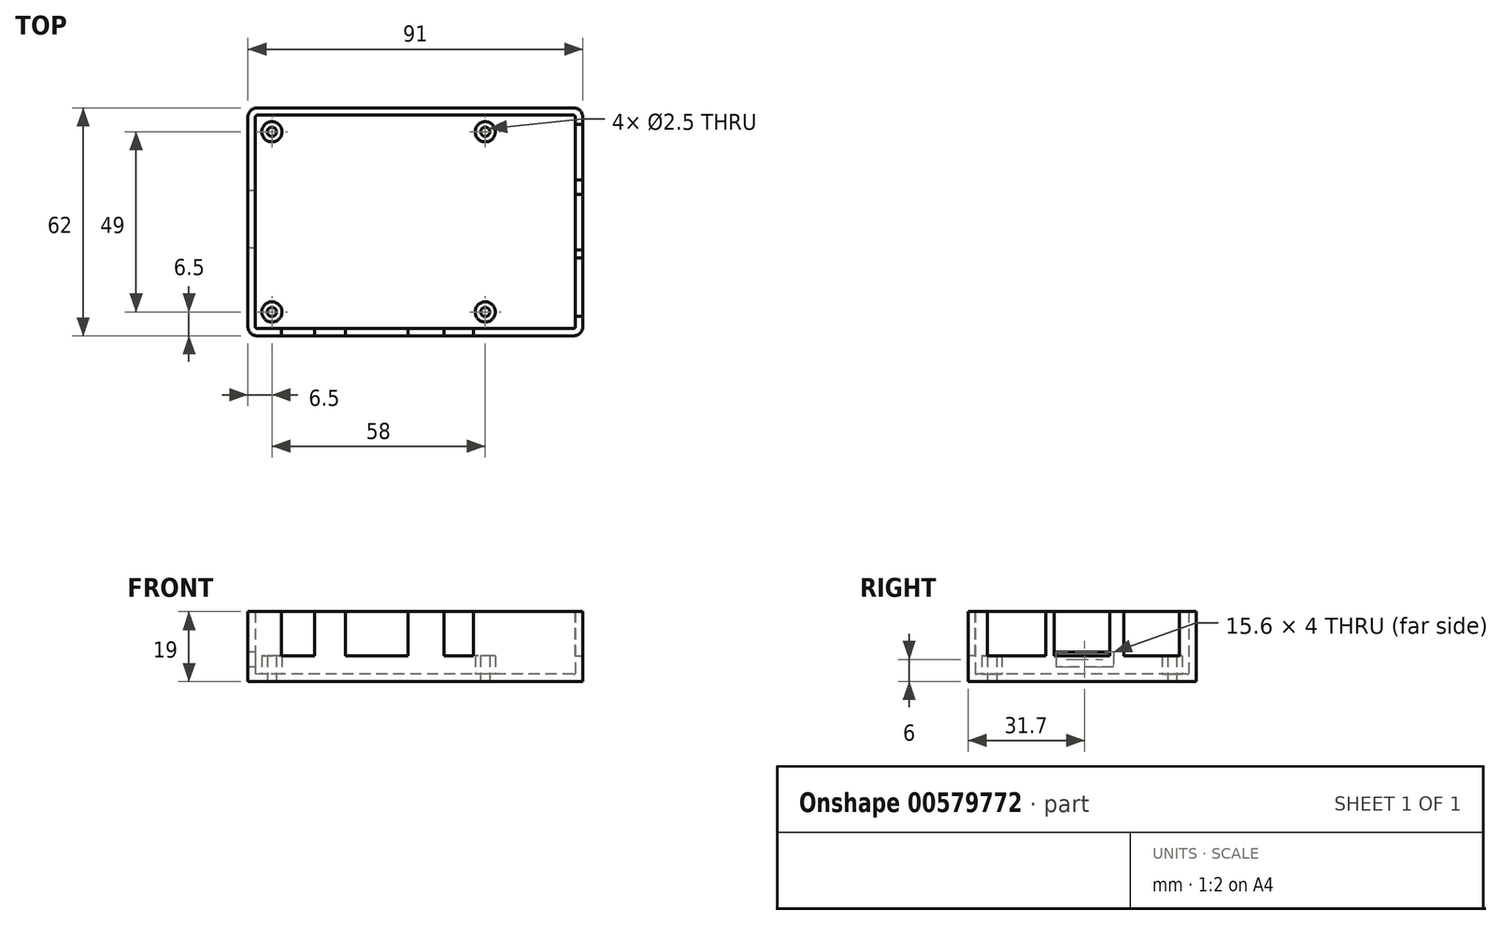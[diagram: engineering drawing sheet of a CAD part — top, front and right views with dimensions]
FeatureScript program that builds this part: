
annotation { "Feature Type Name" : "Feature", "Feature Type Description" : "" }
export const myFeature = defineFeature(function(context is Context, id is Id, definition is map)
    precondition{}
    {
        {
            var Q0;
            Q0=qCreatedBy(makeId("Top.planeOp"),FACE);
            var sketch = newSketch(context, id + "F0", { "sketchPlane" : qUnion([Q0])});
            skLineSegment(sketch, "E0.bottom", {"start": v(2.5, 0) * mm, "end": v(88.5, 0) * mm});
            skLineSegment(sketch, "E0.top", {"start": v(2.5, 62) * mm, "end": v(88.5, 62) * mm});
            skLineSegment(sketch, "E0.left", {"start": v(0, 2.5) * mm, "end": v(0, 59.5) * mm});
            skLineSegment(sketch, "E0.right", {"start": v(91, 2.5) * mm, "end": v(91, 59.5) * mm});
            skPoint(sketch, "E1.visualSharp", {"position": v(0, 62) * mm});
            skArc(sketch, "E1.filletArc", {"start": v(2.5, 62) * mm, "mid": v(0.73, 61.27) * mm, "end": v(0, 59.5) * mm});
            skPoint(sketch, "E2.visualSharp", {"position": v(91, 62) * mm});
            skArc(sketch, "E2.filletArc", {"start": v(91, 59.5) * mm, "mid": v(90.27, 61.27) * mm, "end": v(88.5, 62) * mm});
            skPoint(sketch, "E3.visualSharp", {"position": v(91, 0) * mm});
            skArc(sketch, "E3.filletArc", {"start": v(88.5, 0) * mm, "mid": v(90.27, 0.73) * mm, "end": v(91, 2.5) * mm});
            skPoint(sketch, "E4.visualSharp", {"position": v(0, 0) * mm});
            skArc(sketch, "E4.filletArc", {"start": v(0, 2.5) * mm, "mid": v(0.73, 0.73) * mm, "end": v(2.5, 0) * mm});
            skLineSegment(sketch, "E5.0", {"start": v(2, 2) * mm, "end": v(2, 60) * mm});
            skLineSegment(sketch, "E5.1", {"start": v(2, 2) * mm, "end": v(89, 2) * mm});
            skLineSegment(sketch, "E5.2", {"start": v(89, 2) * mm, "end": v(89, 60) * mm});
            skLineSegment(sketch, "E5.3", {"start": v(2, 60) * mm, "end": v(89, 60) * mm});
            skSolve(sketch);
        }
        {
            var Q0;
            Q0=makeQuery(id+"F0.imprint","IMPRINT",FACE,{"disambiguationData":[TD([[makeQuery(id+"F0.imprint","IMPRINT",EDGE,{"derivedFrom":sQuery(id+"F0.wireOp",EDGE,"E5.0")}),-1.0]])]});
            var Q1;
            Q1=makeQuery(id+"F0.imprint","IMPRINT",FACE,{"disambiguationData":[TD([[makeQuery(id+"F0.imprint","IMPRINT",EDGE,{"derivedFrom":sQuery(id+"F0.wireOp",EDGE,"E0.bottom")}),1.0]])]});
            extrude(context, id + "F1", {"entities" : qUnion([Q0, Q1]), "depth" : 2 * mm, "offsetDistance" : 25 * mm});
        }
        {
            var Q0;
            Q0 = qSketchRegion(id + "F0", true);
            extrude(context, id + "F2", {"entities" : qUnion([Q0]), "operationType" : NewBodyOperationType.ADD, "depth" : 19 * mm, "offsetDistance" : 25 * mm});
        }
        {
            var Q0;
            Q0=makeQuery(id+"F1.opExtrude","CAP_FACE",FACE,{"disambiguationData":[OSD([sQuery(id+"F0.wireOp",EDGE,"E0.bottom"),sQuery(id+"F0.wireOp",EDGE,"E0.top"),sQuery(id+"F0.wireOp",EDGE,"E0.left"),sQuery(id+"F0.wireOp",EDGE,"E0.right"),sQuery(id+"F0.wireOp",EDGE,"E1.filletArc"),sQuery(id+"F0.wireOp",EDGE,"E2.filletArc"),sQuery(id+"F0.wireOp",EDGE,"E3.filletArc"),sQuery(id+"F0.wireOp",EDGE,"E4.filletArc")])],"isStart":false});
            var sketch = newSketch(context, id + "F3", { "sketchPlane" : qUnion([Q0])});
            skCircle(sketch, "E6", {"center": v(6.5, 55.5) * mm, "radius": 2.75 * mm});
            skCircle(sketch, "E7", {"center": v(64.5, 6.5) * mm, "radius": 2.75 * mm});
            skCircle(sketch, "E8", {"center": v(6.5, 6.5) * mm, "radius": 2.75 * mm});
            skCircle(sketch, "E9", {"center": v(64.5, 55.5) * mm, "radius": 2.75 * mm});
            skCircle(sketch, "E10", {"center": v(6.5, 55.5) * mm, "radius": 1.25 * mm});
            skCircle(sketch, "E11", {"center": v(64.5, 55.5) * mm, "radius": 1.25 * mm});
            skCircle(sketch, "E12", {"center": v(64.5, 6.5) * mm, "radius": 1.25 * mm});
            skCircle(sketch, "E13", {"center": v(6.5, 6.5) * mm, "radius": 1.25 * mm});
            skSolve(sketch);
        }
        {
            var Q0;
            Q0 = qSketchRegion(id + "F3", true);
            extrude(context, id + "F4", {"entities" : qUnion([Q0]), "operationType" : NewBodyOperationType.ADD, "depth" : 5 * mm, "offsetDistance" : 25 * mm});
        }
        {
            var Q0;
            Q0=makeQuery(id+"F2.opExtrude","CAP_FACE",FACE,{"disambiguationData":[OSD([sQuery(id+"F0.wireOp",EDGE,"E0.bottom"),sQuery(id+"F0.wireOp",EDGE,"E0.top"),sQuery(id+"F0.wireOp",EDGE,"E0.left"),sQuery(id+"F0.wireOp",EDGE,"E0.right"),sQuery(id+"F0.wireOp",EDGE,"E1.filletArc"),sQuery(id+"F0.wireOp",EDGE,"E2.filletArc"),sQuery(id+"F0.wireOp",EDGE,"E3.filletArc"),sQuery(id+"F0.wireOp",EDGE,"E4.filletArc"),sQuery(id+"F0.wireOp",EDGE,"E5.0"),sQuery(id+"F0.wireOp",EDGE,"E5.1"),sQuery(id+"F0.wireOp",EDGE,"E5.2"),sQuery(id+"F0.wireOp",EDGE,"E5.3")])],"isStart":false});
            var sketch = newSketch(context, id + "F5", { "sketchPlane" : qUnion([Q0])});
            skLineSegment(sketch, "E14.bottom", {"start": v(9.05, 0) * mm, "end": v(18.05, 0) * mm});
            skLineSegment(sketch, "E14.top", {"start": v(9.05, 2) * mm, "end": v(18.05, 2) * mm});
            skLineSegment(sketch, "E14.left", {"start": v(9.05, 0) * mm, "end": v(9.05, 2) * mm});
            skLineSegment(sketch, "E14.right", {"start": v(18.05, 0) * mm, "end": v(18.05, 2) * mm});
            skLineSegment(sketch, "E15.bottom", {"start": v(26.5, 2) * mm, "end": v(43.5, 2) * mm});
            skLineSegment(sketch, "E15.top", {"start": v(26.5, 0) * mm, "end": v(43.5, 0) * mm});
            skLineSegment(sketch, "E15.left", {"start": v(26.5, 2) * mm, "end": v(26.5, 0) * mm});
            skLineSegment(sketch, "E15.right", {"start": v(43.5, 2) * mm, "end": v(43.5, 0) * mm});
            skLineSegment(sketch, "E16.bottom", {"start": v(53.25, 2) * mm, "end": v(61.25, 2) * mm});
            skLineSegment(sketch, "E16.top", {"start": v(53.25, 0) * mm, "end": v(61.25, 0) * mm});
            skLineSegment(sketch, "E16.left", {"start": v(53.25, 2) * mm, "end": v(53.25, 0) * mm});
            skLineSegment(sketch, "E16.right", {"start": v(61.25, 2) * mm, "end": v(61.25, 0) * mm});
            skLineSegment(sketch, "E17.bottom", {"start": v(89, 21.2) * mm, "end": v(91, 21.2) * mm});
            skLineSegment(sketch, "E17.top", {"start": v(89, 5.3) * mm, "end": v(91, 5.3) * mm});
            skLineSegment(sketch, "E17.left", {"start": v(89, 21.2) * mm, "end": v(89, 5.3) * mm});
            skLineSegment(sketch, "E17.right", {"start": v(91, 21.2) * mm, "end": v(91, 5.3) * mm});
            skLineSegment(sketch, "E18.bottom", {"start": v(89, 23.4) * mm, "end": v(91, 23.4) * mm});
            skLineSegment(sketch, "E18.top", {"start": v(89, 38.5) * mm, "end": v(91, 38.5) * mm});
            skLineSegment(sketch, "E18.left", {"start": v(89, 23.4) * mm, "end": v(89, 38.5) * mm});
            skLineSegment(sketch, "E18.right", {"start": v(91, 23.4) * mm, "end": v(91, 38.5) * mm});
            skLineSegment(sketch, "E19.bottom", {"start": v(89, 42.4) * mm, "end": v(91, 42.4) * mm});
            skLineSegment(sketch, "E19.top", {"start": v(89, 57.5) * mm, "end": v(91, 57.5) * mm});
            skLineSegment(sketch, "E19.left", {"start": v(89, 42.4) * mm, "end": v(89, 57.5) * mm});
            skLineSegment(sketch, "E19.right", {"start": v(91, 42.4) * mm, "end": v(91, 57.5) * mm});
            skSolve(sketch);
        }
        {
            var Q0;
            Q0 = qSketchRegion(id + "F5", true);
            extrude(context, id + "F6", {"entities" : qUnion([Q0]), "operationType" : NewBodyOperationType.REMOVE, "oppositeDirection" : true, "depth" : 12 * mm, "offsetDistance" : 25 * mm});
        }
        {
            var Q0;
            {var subQ0=sQuery(id+"F0.wireOp",EDGE,"E0.left");Q0=makeQuery(id+"F2.boolean.opBoolean","MERGE",FACE,{"derivedFrom":[makeQuery(id+"F1.opExtrude","SWEPT_FACE",FACE,{"disambiguationData":[OSD([subQ0])]}),makeQuery(id+"F2.opExtrude","SWEPT_FACE",FACE,{"disambiguationData":[OSD([subQ0])]})]});}
            var sketch = newSketch(context, id + "F7", { "sketchPlane" : qUnion([Q0])});
            skLineSegment(sketch, "E20.bottom", {"start": v(-39.5, 8) * mm, "end": v(-23.9, 8) * mm});
            skLineSegment(sketch, "E20.top", {"start": v(-39.5, 4) * mm, "end": v(-23.9, 4) * mm});
            skLineSegment(sketch, "E20.left", {"start": v(-39.5, 8) * mm, "end": v(-39.5, 4) * mm});
            skLineSegment(sketch, "E20.right", {"start": v(-23.9, 8) * mm, "end": v(-23.9, 4) * mm});
            skSolve(sketch);
        }
        {
            var Q0;
            Q0 = qSketchRegion(id + "F7", true);
            extrude(context, id + "F8", {"entities" : qUnion([Q0]), "operationType" : NewBodyOperationType.REMOVE, "oppositeDirection" : true, "depth" : 5 * mm, "offsetDistance" : 25 * mm});
        }
        {
            var Q0;
            Q0=makeQuery(id+"F2.opExtrude","SWEPT_EDGE",EDGE,{"disambiguationData":[OSD([sQuery(id+"F0.wireOp",EDGE,"E5.0"),sQuery(id+"F0.wireOp",EDGE,"E5.3")])]});
            var Q1;
            Q1=makeQuery(id+"F2.opExtrude","SWEPT_EDGE",EDGE,{"disambiguationData":[OSD([sQuery(id+"F0.wireOp",EDGE,"E5.2"),sQuery(id+"F0.wireOp",EDGE,"E5.3")])]});
            var Q2;
            Q2=makeQuery(id+"F2.opExtrude","SWEPT_EDGE",EDGE,{"disambiguationData":[OSD([sQuery(id+"F0.wireOp",EDGE,"E5.0"),sQuery(id+"F0.wireOp",EDGE,"E5.1")])]});
            var Q3;
            Q3=makeQuery(id+"F2.opExtrude","SWEPT_EDGE",EDGE,{"disambiguationData":[OSD([sQuery(id+"F0.wireOp",EDGE,"E5.1"),sQuery(id+"F0.wireOp",EDGE,"E5.2")])]});
            fillet(context, id + "F9", {"entities" : qUnion([Q0, Q1, Q2, Q3]), "radius" : 0.5 * mm, "tangentPropagation" : true, "allowEdgeOverflow" : false});
        }
        {
            var Q0;
            Q0=makeQuery(id+"F4.boolean.opBoolean","SPLIT",FACE,{"disambiguationData":[TD([makeQuery(id+"F4.opExtrude","SWEPT_FACE",FACE,{"disambiguationData":[OSD([sQuery(id+"F3.wireOp",EDGE,"E10")])]})])],"derivedFrom":makeQuery(id+"F1.opExtrude","CAP_FACE",FACE,{"disambiguationData":[OSD([sQuery(id+"F0.wireOp",EDGE,"E0.bottom"),sQuery(id+"F0.wireOp",EDGE,"E0.top"),sQuery(id+"F0.wireOp",EDGE,"E0.left"),sQuery(id+"F0.wireOp",EDGE,"E0.right"),sQuery(id+"F0.wireOp",EDGE,"E1.filletArc"),sQuery(id+"F0.wireOp",EDGE,"E2.filletArc"),sQuery(id+"F0.wireOp",EDGE,"E3.filletArc"),sQuery(id+"F0.wireOp",EDGE,"E4.filletArc")])],"isStart":false})});
            var Q1;
            Q1=makeQuery(id+"F4.boolean.opBoolean","SPLIT",FACE,{"disambiguationData":[TD([makeQuery(id+"F4.opExtrude","SWEPT_FACE",FACE,{"disambiguationData":[OSD([sQuery(id+"F3.wireOp",EDGE,"E11")])]})])],"derivedFrom":makeQuery(id+"F1.opExtrude","CAP_FACE",FACE,{"disambiguationData":[OSD([sQuery(id+"F0.wireOp",EDGE,"E0.bottom"),sQuery(id+"F0.wireOp",EDGE,"E0.top"),sQuery(id+"F0.wireOp",EDGE,"E0.left"),sQuery(id+"F0.wireOp",EDGE,"E0.right"),sQuery(id+"F0.wireOp",EDGE,"E1.filletArc"),sQuery(id+"F0.wireOp",EDGE,"E2.filletArc"),sQuery(id+"F0.wireOp",EDGE,"E3.filletArc"),sQuery(id+"F0.wireOp",EDGE,"E4.filletArc")])],"isStart":false})});
            var Q2;
            Q2=makeQuery(id+"F4.boolean.opBoolean","SPLIT",FACE,{"disambiguationData":[TD([makeQuery(id+"F4.opExtrude","SWEPT_FACE",FACE,{"disambiguationData":[OSD([sQuery(id+"F3.wireOp",EDGE,"E12")])]})])],"derivedFrom":makeQuery(id+"F1.opExtrude","CAP_FACE",FACE,{"disambiguationData":[OSD([sQuery(id+"F0.wireOp",EDGE,"E0.bottom"),sQuery(id+"F0.wireOp",EDGE,"E0.top"),sQuery(id+"F0.wireOp",EDGE,"E0.left"),sQuery(id+"F0.wireOp",EDGE,"E0.right"),sQuery(id+"F0.wireOp",EDGE,"E1.filletArc"),sQuery(id+"F0.wireOp",EDGE,"E2.filletArc"),sQuery(id+"F0.wireOp",EDGE,"E3.filletArc"),sQuery(id+"F0.wireOp",EDGE,"E4.filletArc")])],"isStart":false})});
            var Q3;
            Q3=makeQuery(id+"F4.boolean.opBoolean","SPLIT",FACE,{"disambiguationData":[TD([makeQuery(id+"F4.opExtrude","SWEPT_FACE",FACE,{"disambiguationData":[OSD([sQuery(id+"F3.wireOp",EDGE,"E13")])]})])],"derivedFrom":makeQuery(id+"F1.opExtrude","CAP_FACE",FACE,{"disambiguationData":[OSD([sQuery(id+"F0.wireOp",EDGE,"E0.bottom"),sQuery(id+"F0.wireOp",EDGE,"E0.top"),sQuery(id+"F0.wireOp",EDGE,"E0.left"),sQuery(id+"F0.wireOp",EDGE,"E0.right"),sQuery(id+"F0.wireOp",EDGE,"E1.filletArc"),sQuery(id+"F0.wireOp",EDGE,"E2.filletArc"),sQuery(id+"F0.wireOp",EDGE,"E3.filletArc"),sQuery(id+"F0.wireOp",EDGE,"E4.filletArc")])],"isStart":false})});
            var Q4;
            Q4=makeQuery(id+"F1.opExtrude","CAP_FACE",FACE,{"disambiguationData":[OSD([sQuery(id+"F0.wireOp",EDGE,"E0.bottom"),sQuery(id+"F0.wireOp",EDGE,"E0.top"),sQuery(id+"F0.wireOp",EDGE,"E0.left"),sQuery(id+"F0.wireOp",EDGE,"E0.right"),sQuery(id+"F0.wireOp",EDGE,"E1.filletArc"),sQuery(id+"F0.wireOp",EDGE,"E2.filletArc"),sQuery(id+"F0.wireOp",EDGE,"E3.filletArc"),sQuery(id+"F0.wireOp",EDGE,"E4.filletArc")])],"isStart":true});
            extrude(context, id + "F10", {"entities" : qUnion([Q0, Q1, Q2, Q3]), "operationType" : NewBodyOperationType.REMOVE, "endBound" : BoundingType.UP_TO_SURFACE, "oppositeDirection" : true, "depth" : 25 * mm, "endBoundEntityFace" : qUnion([Q4]), "offsetDistance" : 25 * mm});
        }
    });
